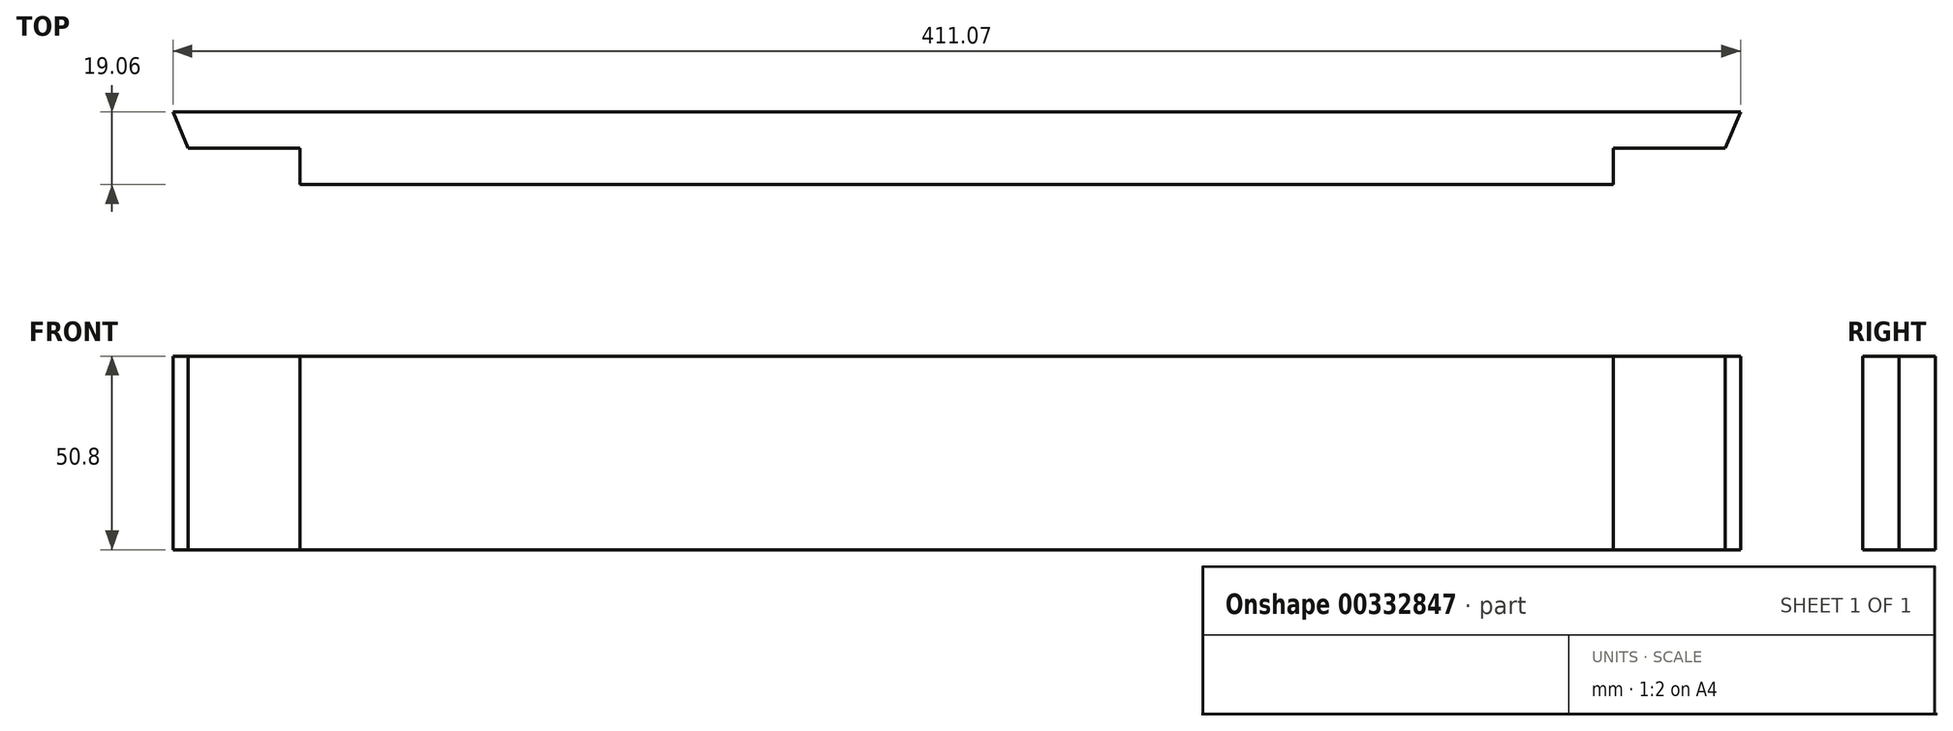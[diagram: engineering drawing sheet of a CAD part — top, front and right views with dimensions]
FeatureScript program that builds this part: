
annotation { "Feature Type Name" : "Feature", "Feature Type Description" : "" }
export const myFeature = defineFeature(function(context is Context, id is Id, definition is map)
    precondition{}
    {
        {
            var Q0;
            Q0=qCreatedBy(makeId("Top.planeOp"),FACE);
            var sketch = newSketch(context, id + "F0", { "sketchPlane" : qUnion([Q0])});
            skLineSegment(sketch, "E0", {"start": v(25.4, -9.53) * mm, "end": v(369.89, -9.53) * mm});
            skLineSegment(sketch, "E1", {"start": v(399.23, 0) * mm, "end": v(403.18, 9.52) * mm});
            skLineSegment(sketch, "E2", {"start": v(403.18, 9.52) * mm, "end": v(-7.9, 9.53) * mm});
            skLineSegment(sketch, "E3", {"start": v(-7.9, 9.53) * mm, "end": v(-3.95, 0) * mm});
            skLineSegment(sketch, "E4.top", {"start": v(369.89, 0) * mm, "end": v(399.23, 0) * mm});
            skLineSegment(sketch, "E4.left", {"start": v(369.89, -9.53) * mm, "end": v(369.89, 0) * mm});
            skPoint(sketch, "E5.orphan", {"position": v(395.29, -9.53) * mm});
            skLineSegment(sketch, "E6.top", {"start": v(25.4, 0) * mm, "end": v(-3.95, 0) * mm});
            skLineSegment(sketch, "E6.left", {"start": v(25.4, -9.53) * mm, "end": v(25.4, 0) * mm});
            skPoint(sketch, "E7.orphan", {"position": v(0, -9.53) * mm});
            skSolve(sketch);
        }
        {
            var Q0;
            Q0=makeQuery(id+"F0.imprint","IMPRINT",FACE,{"disambiguationData":[TD([[makeQuery(id+"F0.imprint","IMPRINT",EDGE,{"derivedFrom":sQuery(id+"F0.wireOp",EDGE,"E0")}),1.0]])]});
            extrude(context, id + "F1", {"entities" : qUnion([Q0]), "endBound" : BoundingType.SYMMETRIC, "depth" : 50.8 * mm});
        }
    });
